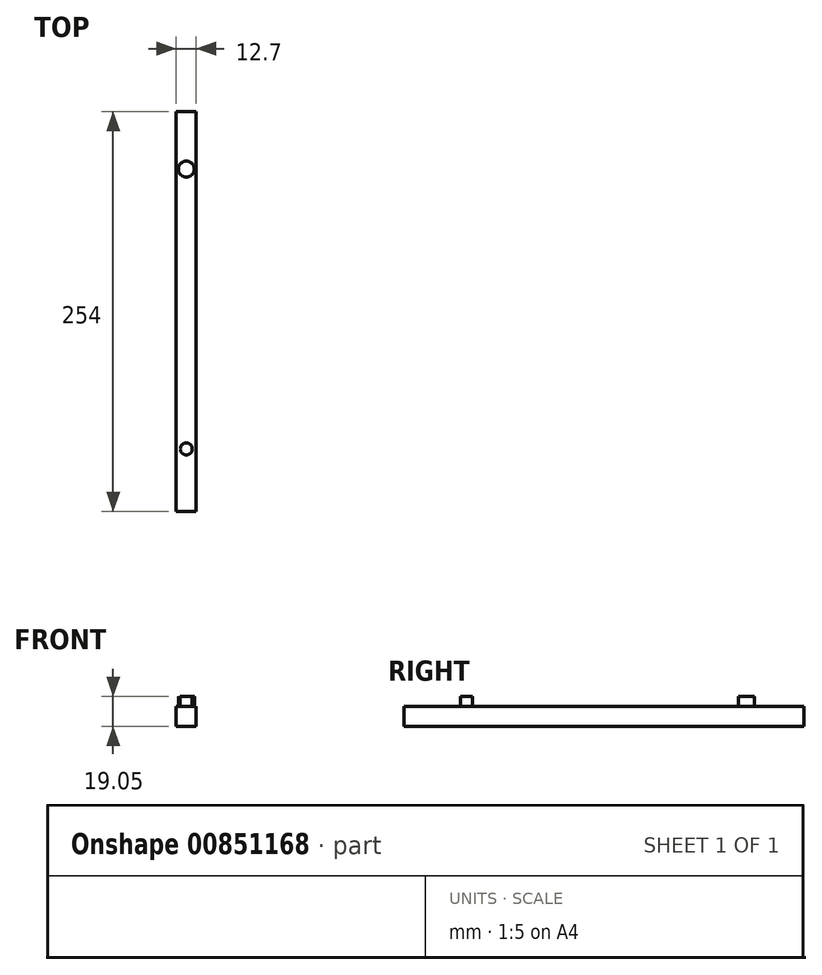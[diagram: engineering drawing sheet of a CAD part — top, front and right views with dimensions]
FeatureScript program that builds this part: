
annotation { "Feature Type Name" : "Feature", "Feature Type Description" : "" }
export const myFeature = defineFeature(function(context is Context, id is Id, definition is map)
    precondition{}
    {
        {
            var Q0;
            Q0=qCreatedBy(makeId("Front.planeOp"),FACE);
            var sketch = newSketch(context, id + "F0", { "sketchPlane" : qUnion([Q0])});
            skLineSegment(sketch, "E0.bottom", {"start": v(6.35, 6.35) * mm, "end": v(-6.35, 6.35) * mm});
            skLineSegment(sketch, "E0.top", {"start": v(6.35, -6.35) * mm, "end": v(-6.35, -6.35) * mm});
            skLineSegment(sketch, "E0.left", {"start": v(6.35, 6.35) * mm, "end": v(6.35, -6.35) * mm});
            skLineSegment(sketch, "E0.right", {"start": v(-6.35, 6.35) * mm, "end": v(-6.35, -6.35) * mm});
            skPoint(sketch, "E0.middle", {"position": v(0, 0) * mm});
            skSolve(sketch);
        }
        {
            var Q0;
            Q0 = qSketchRegion(id + "F0", true);
            extrude(context, id + "F1", {"entities" : qUnion([Q0]), "depth" : 254 * mm, "offsetDistance" : 25.4 * mm});
        }
        {
            var Q0;
            Q0=qCreatedBy(makeId("Top.planeOp"),FACE);
            var sketch = newSketch(context, id + "F2", { "sketchPlane" : qUnion([Q0])});
            skCircle(sketch, "E1", {"center": v(0, -36.6) * mm, "radius": 5.08 * mm});
            skCircle(sketch, "E2", {"center": v(0, -214.31) * mm, "radius": 3.81 * mm});
            skSolve(sketch);
        }
        {
            var Q0;
            Q0 = qSketchRegion(id + "F2", true);
            extrude(context, id + "F3", {"entities" : qUnion([Q0]), "operationType" : NewBodyOperationType.ADD, "depth" : 12.7 * mm, "hasOffset" : true, "offsetDistance" : 5.08 * mm});
        }
    });
